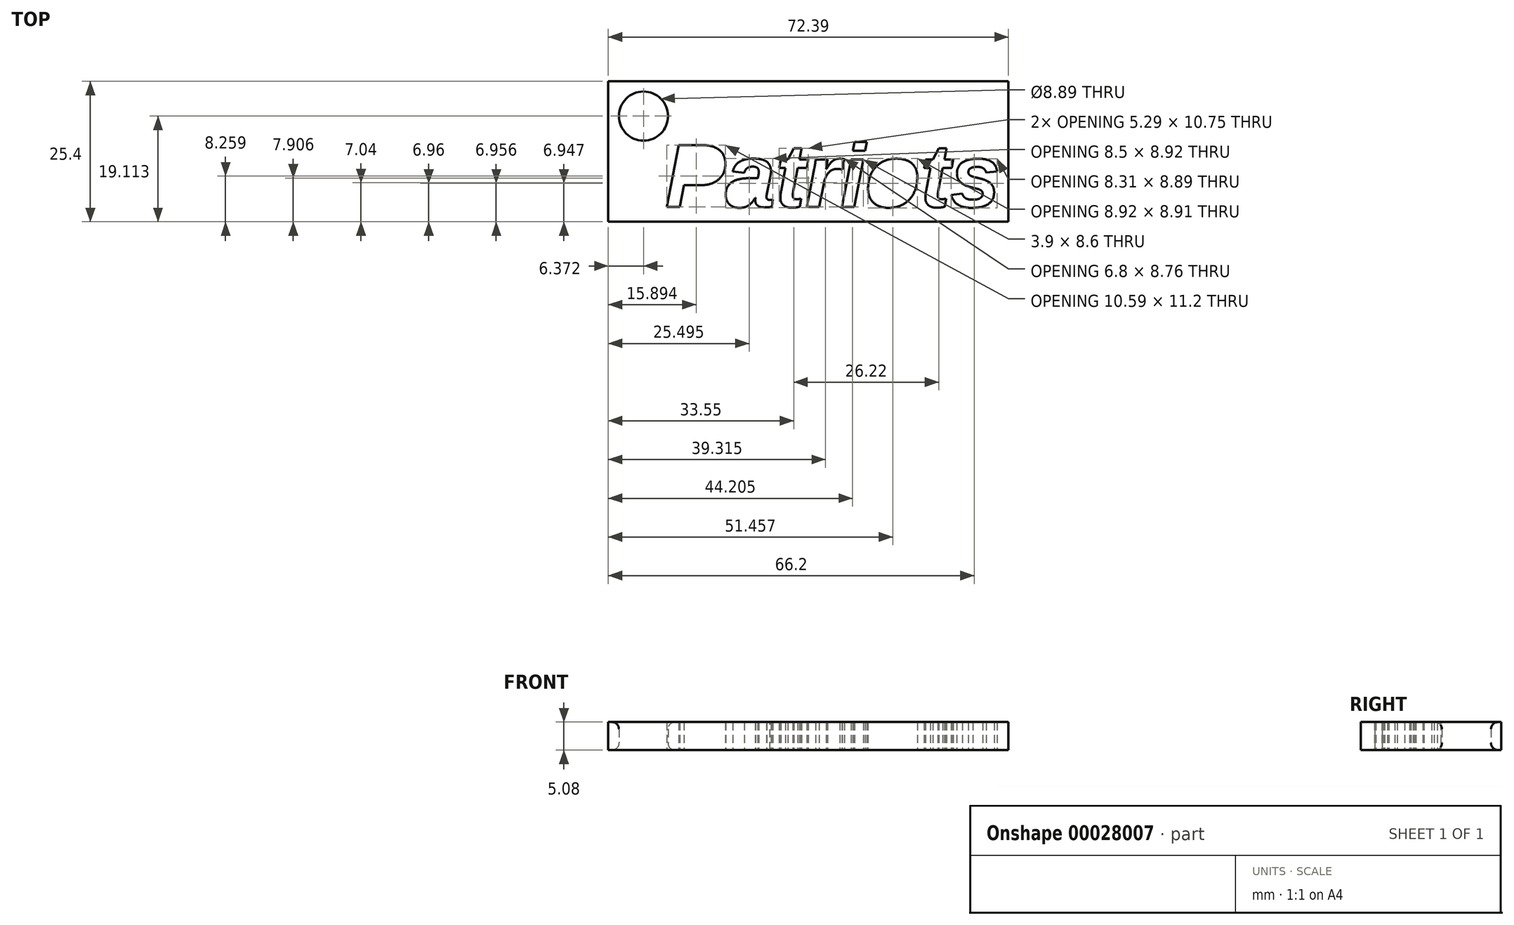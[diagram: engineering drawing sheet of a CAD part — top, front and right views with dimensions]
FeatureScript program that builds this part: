
annotation { "Feature Type Name" : "Feature", "Feature Type Description" : "" }
export const myFeature = defineFeature(function(context is Context, id is Id, definition is map)
    precondition{}
    {
        {
            var Q0;
            Q0=qCreatedBy(makeId("Top.planeOp"),FACE);
            var sketch = newSketch(context, id + "F0", { "sketchPlane" : qUnion([Q0])});
            skText(sketch, "E0", { "text": "Patriots", "fontName": "Arimo-BoldItalic.ttf"});
            skLineSegment(sketch, "E1.bottom", {"start": v(34.63, -4.42) * mm, "end": v(-37.76, -4.42) * mm});
            skLineSegment(sketch, "E1.top", {"start": v(34.63, 20.98) * mm, "end": v(-37.76, 20.98) * mm});
            skLineSegment(sketch, "E1.left", {"start": v(34.63, -4.42) * mm, "end": v(34.63, 20.98) * mm});
            skLineSegment(sketch, "E1.right", {"start": v(-37.76, -4.42) * mm, "end": v(-37.76, 20.98) * mm});
            skCircle(sketch, "E2", {"center": v(-31.39, 14.7) * mm, "radius": 4.45 * mm});
            const initialGuessF0  = {"E0": [-0.02745, -0.00176, 1, 0, 0.01172]};
            skSetInitialGuess(sketch, initialGuessF0);
            skSolve(sketch);
        }
        {
            var Q0;
            Q0 = qSketchRegion(id + "F0", true);
            extrude(context, id + "F1", {"entities" : qUnion([Q0]), "depth" : 5.08 * mm});
        }
        {
            var Q0;
            Q0=makeQuery(id+"F1.opExtrude","CAP_EDGE",EDGE,{"disambiguationData":[OSD([sQuery(id+"F0.wireOp",EDGE,"E2")])],"isStart":false});
            var Q1;
            Q1=makeQuery(id+"F1.opExtrude","CAP_EDGE",EDGE,{"disambiguationData":[OSD([sQuery(id+"F0.wireOp",EDGE,"E2")])],"isStart":true});
            fillet(context, id + "F2", {"entities" : qUnion([Q0, Q1]), "radius" : 1.27 * mm, "tangentPropagation" : true, "allowEdgeOverflow" : false});
        }
    });
